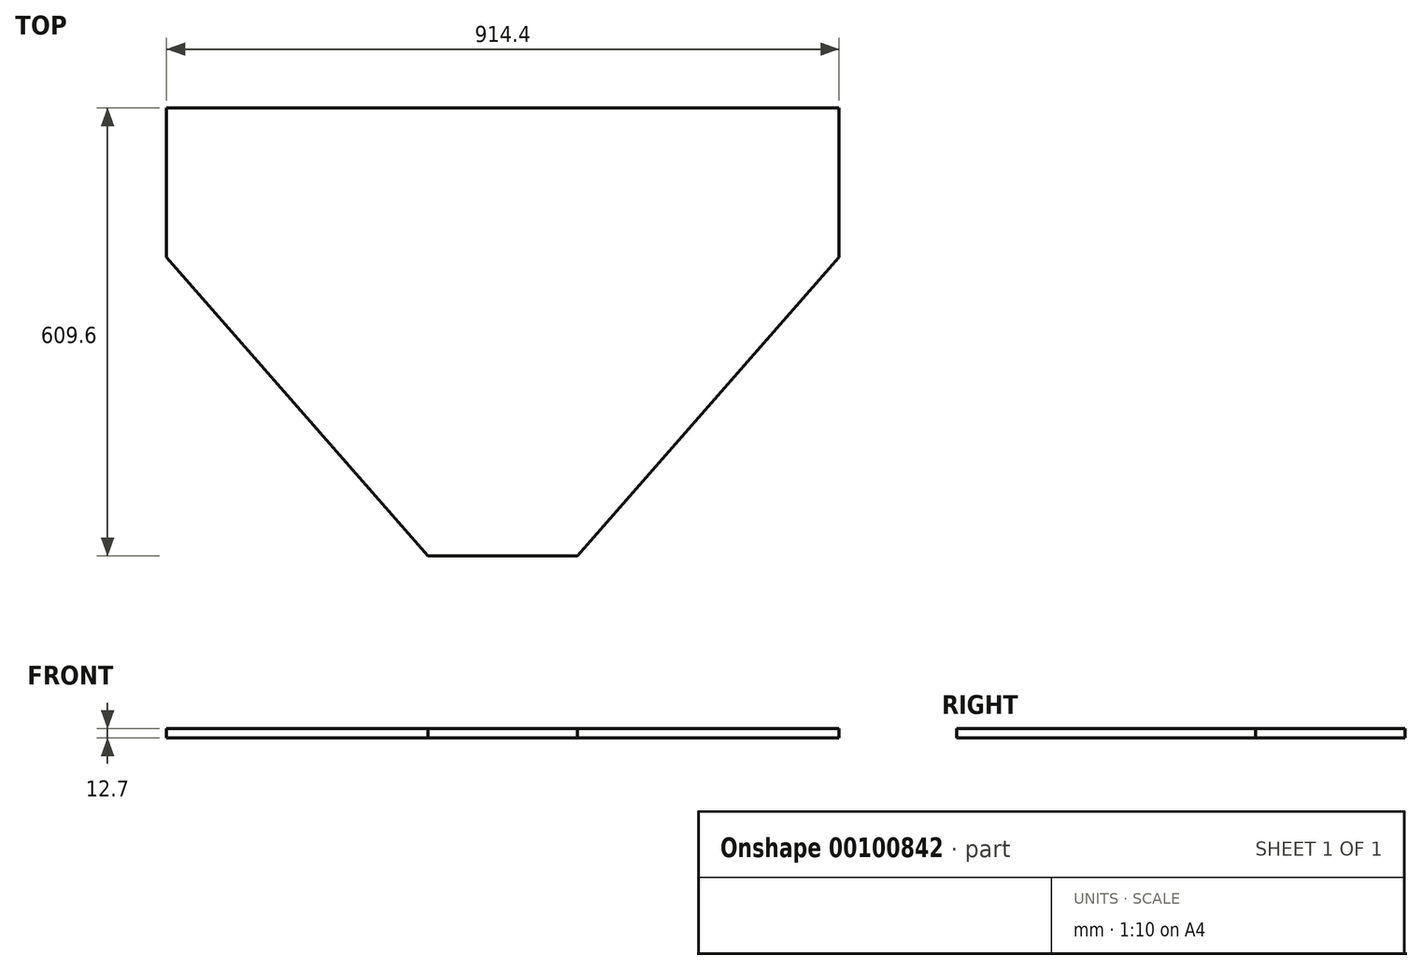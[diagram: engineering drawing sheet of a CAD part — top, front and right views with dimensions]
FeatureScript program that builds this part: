
annotation { "Feature Type Name" : "Feature", "Feature Type Description" : "" }
export const myFeature = defineFeature(function(context is Context, id is Id, definition is map)
    precondition{}
    {
        {
            var Q0;
            Q0=qCreatedBy(makeId("Top.planeOp"),FACE);
            var sketch = newSketch(context, id + "F0", { "sketchPlane" : qUnion([Q0])});
            skLineSegment(sketch, "E0.bottom", {"start": v(355.6, 0) * mm, "end": v(558.8, 0) * mm});
            skLineSegment(sketch, "E0.top", {"start": v(0, 609.6) * mm, "end": v(914.4, 609.6) * mm});
            skLineSegment(sketch, "E0.left", {"start": v(0, 406.4) * mm, "end": v(0, 609.6) * mm});
            skLineSegment(sketch, "E0.right", {"start": v(914.4, 406.4) * mm, "end": v(914.4, 609.6) * mm});
            skLineSegment(sketch, "E1", {"start": v(0, 406.4) * mm, "end": v(355.6, 0) * mm});
            skLineSegment(sketch, "E2", {"start": v(914.4, 406.4) * mm, "end": v(558.8, 0) * mm});
            skPoint(sketch, "E3.orphan", {"position": v(0, 0) * mm});
            skPoint(sketch, "E4.orphan", {"position": v(914.4, 0) * mm});
            skSolve(sketch);
        }
        {
            var Q0;
            Q0=makeQuery(id+"F0.imprint","IMPRINT",FACE,{"disambiguationData":[TD([[makeQuery(id+"F0.imprint","IMPRINT",EDGE,{"derivedFrom":sQuery(id+"F0.wireOp",EDGE,"E0.bottom")}),1.0]])]});
            extrude(context, id + "F1", {"entities" : qUnion([Q0]), "depth" : 12.7 * mm});
        }
    });
